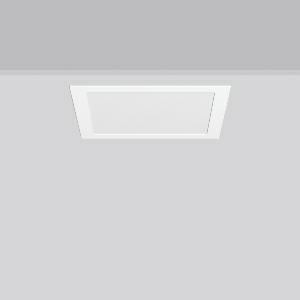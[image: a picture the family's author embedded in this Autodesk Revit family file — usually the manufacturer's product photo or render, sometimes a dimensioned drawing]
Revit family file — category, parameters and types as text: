
# Revit family: toledo_flat_square_e_901488_002_1_76_7786
name_source: partatom
category: Lighting Fixtures
units: mm (PartAtom-declared; Revit-internal decimal feet)

## family parameters
Cut with Voids When Loaded = No
Host = Face
Light Source = No
Part Type = Normal
Room Calculation Point = No
Round Connector Dimension = Use Diameter
Shared = No

## types (1)
- TOLEDO FLAT square E (1 x LED Modul 840, 2250 lm, 4000)
    Apparent Load = 21 VA
    CIE Flux Codes = 49 80 96 100 100
    Color Rendering = 80
    Color Temperature = 4000
    Default Elevation = 1800 mm
    Description = Series: TOLEDO FLAT square
Ultra thin recessed downlight. Housing: die-cast aluminium. Light guide and diffuser made of non-yellowing PMMA, opal matt. Ceiling installation with spring system. Mounting depth depends on ceiling strength. Suitable for through-wiring with separately available accessories. Surface mounted housing as accessory for all sizes. Retrofittable decorative cylinders made of chintz fabric as accessory, optional with satin finish plastic diffuser. Through-wiring box (5 pole) available as accessory. 
Colour: white
Length: 300 mm
Width: 300 mm
Height: 3 mm
Cut-out length: 280 mm
Cut-out width: 280 mm
Recess height: 31-56 mm
Luminaire: recess height: 31-51 mm
Lamp: LED
Socket: without socket
Colour temperature: 4000K
Colour rendering index (CRI): 80
System power: 21 W
Rated luminous flux: 2250 lm
Luminous efficiency: 107 lm/W
Control gear: Converter, dimmable, DALI
Protection class: II
Type of protection: IP 54
    Height = 0 mm  [stored 0 ft]
    Lamp = 1 x LED Modul 840
    Lamp Light Flux = 2250 lm
    Lamp count = 1
    Length = 300 mm
    Lifetime = 50000 h
    Luminous efficacy = 107 lm/W
    Manufacturer = RZB
    ModVariant = No
    Model = 901488.002.1.76
    Mounting Place = Ceiling
    Mounting Type = Recessed
    Number of Poles = 1
    OnlyDefault = Yes
    Power Factor = 1
    Product Name = TOLEDO FLAT square E
    Product group = Recessed downlights
    ProductGroupID = 402
    Protection Class = Protection class II
    Protection Degree = IP 20
    RLX_Detail_Level = 1
    RLX_Emergency_Light_Flux = 0 lm
    RLX_Emergency_Type = 0
    RLX_Emergency_Type_DB = No
    RlxData = <blob elided: 60981 chars, md5=cb5672d3>
    Socket = socket
    Standby Power = 0 W
    System Light Flux = 2250 lm
    System Power = 21 W
    Type Comments = Product without accessories
    Type Image = 901488.002.jpg
    URL = http://relux.com
    VarID = ---
    Voltage = 230 V
    Voltage Range = 220-240 V
    Weight = 0.00 kg
    Width = 300 mm

note: [stored X ft] marks values corroborated as IEEE doubles in the binary element streams (Revit-internal decimal feet)

## geometry (parser evidence)
native form markers: Blend x4, Sweep x10
no freeform markers — native parametric forms only
